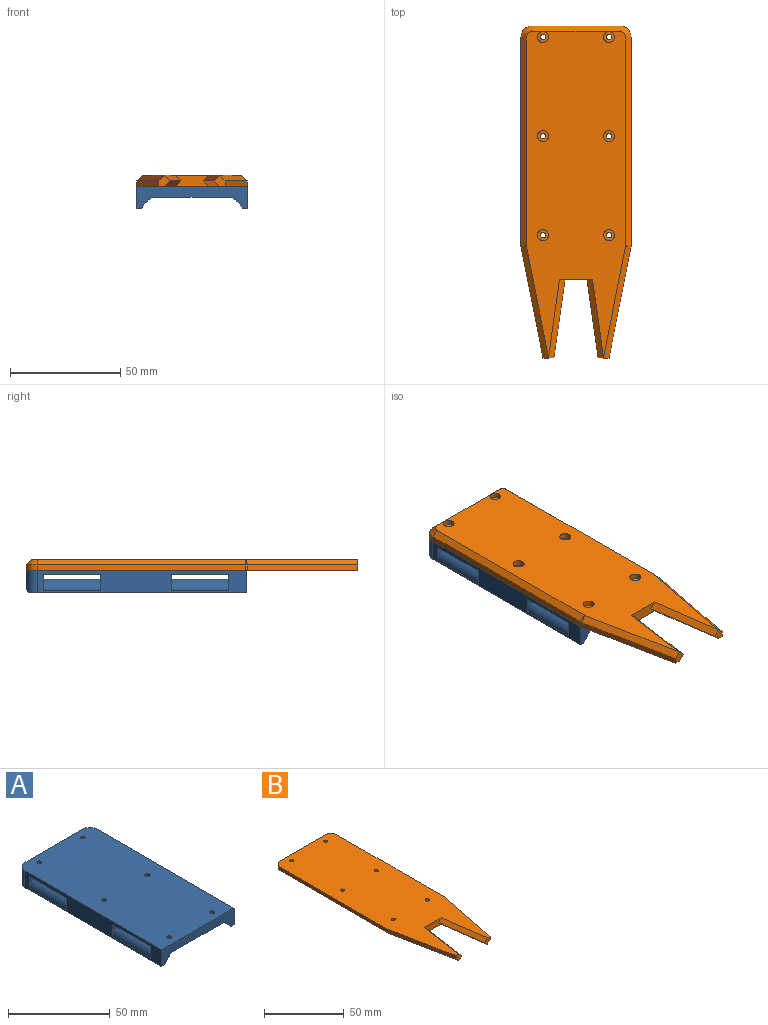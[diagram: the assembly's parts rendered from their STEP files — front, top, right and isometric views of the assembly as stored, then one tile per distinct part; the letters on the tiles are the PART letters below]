
ASSEMBLY  parts=2 mates=1
PART A: 30 faces, bbox 50x100x10.1 mm
  f0: plane 95x10.08mm, normal (1,0,0), area 589.4mm2, adj f4,f7,f15,f16,f17,f18,f20,f21
  f1: plane 95x10.08mm, normal (-1,0,0), area 589.4mm2, adj f4,f7,f15,f16,f17,f18,f20,f21
  f2: cylinder r=16.27mm len=100mm, axis (0,1,0), area 704.3mm2, adj f4,f5,f6,f27,f29
  f3: cylinder r=16.27mm len=100mm, axis (0,1,0), area 704.3mm2, adj f4,f5,f6,f26,f28
  f4: plane 50x10.08mm, normal (0,-1,0), area 290.8mm2, adj f0,f1,f2,f3,f6,f7,f26,f27
  f5: plane 40x6.39mm, normal (0,1,0), area 202.4mm2, adj f2,f3,f6,f7,f28,f29
  f6: plane 100x36.44mm, normal (0,0,-1), area 3614mm2, adj f2,f3,f4,f5,f8,f9,f10,f11
  f7: plane 100x50mm, normal (0,0,1), area 4959.8mm2, adj f0,f1,f4,f5,f8,f9,f10,f11
  f8: cylinder r=1.25mm len=5mm, axis (0,0,1), area 39.3mm2, adj f6,f7
  f9: cylinder r=1.25mm len=5mm, axis (0,0,1), area 39.3mm2, adj f6,f7
  f10: cylinder r=1.25mm len=5mm, axis (0,0,1), area 39.3mm2, adj f6,f7
  f11: cylinder r=1.25mm len=5mm, axis (0,0,1), area 39.3mm2, adj f6,f7
  f12: cylinder r=1.25mm len=5mm, axis (0,0,1), area 39.3mm2, adj f6,f7
  f13: cylinder r=1.25mm len=5mm, axis (0,0,1), area 39.3mm2, adj f6,f7
  f14: plane 39.84x26mm, normal (0,0,1), area 1035.8mm2, adj f15,f17,f23,f24
  f15: plane 50x7.08mm, normal (0,-1,0), area 111.1mm2, adj f0,f1,f14,f16,f23,f24
  f16: plane 50x26mm, normal (0,0,-1), area 1300mm2, adj f0,f1,f15,f17
  f17: plane 50x7.08mm, normal (0,1,0), area 111.1mm2, adj f0,f1,f14,f16,f23,f24
  f18: plane 50x7.08mm, normal (0,1,0), area 111.1mm2, adj f0,f1,f19,f21,f22,f25
  f19: plane 39.84x26mm, normal (0,0,1), area 1035.8mm2, adj f18,f20,f22,f25
  f20: plane 50x7.08mm, normal (0,-1,0), area 111.1mm2, adj f0,f1,f19,f21,f22,f25
  f21: plane 50x26mm, normal (0,0,-1), area 1300mm2, adj f0,f1,f18,f20
  f22: cylinder r=5.08mm len=26mm, axis (0,1,0), area 207.5mm2, adj f1,f18,f19,f20
  f23: cylinder r=5.08mm len=26mm, axis (0,1,0), area 207.5mm2, adj f1,f14,f15,f17
  f24: cylinder r=5.08mm len=26mm, axis (0,-1,0), area 207.5mm2, adj f0,f14,f15,f17
  f25: cylinder r=5.08mm len=26mm, axis (0,-1,0), area 207.5mm2, adj f0,f18,f19,f20
  f26: plane 98.97x1.96mm, normal (0,0,-1), area 191.6mm2, adj f0,f3,f4,f28
  f27: plane 98.97x1.96mm, normal (0,0,-1), area 191.6mm2, adj f1,f2,f4,f29
  f28: cylinder r=5mm len=10.08mm, axis (0,0,1), area 72.8mm2, adj f0,f3,f5,f7,f26
  f29: cylinder r=5mm len=10.08mm, axis (0,0,-1), area 72.8mm2, adj f1,f2,f5,f7,f27
PART B: 45 faces, bbox 50x150.8x5 mm
  f0: plane 94.51x2.5mm, normal (-1,0,0), area 236.3mm2, adj f8,f28,f31,f36
  f1: plane 50.31x9.91mm, normal (-0.98,-0.19,0), area 128.2mm2, adj f2,f8,f28,f34
  f2: plane 5x4.96mm, normal (0,-1,0), area 15.5mm2, adj f1,f8,f32,f33,f34
  f3: plane 15.05x5mm, normal (0,-1,0), area 62.6mm2, adj f8,f9,f32,f33,f40,f42
  f4: plane 5x4.96mm, normal (0,-1,0), area 15.5mm2, adj f5,f8,f40,f42,f44
  f5: plane 50.31x9.91mm, normal (0.98,-0.19,0), area 128.2mm2, adj f4,f8,f29,f44
  f6: plane 94.51x2.5mm, normal (1,0,0), area 236.3mm2, adj f8,f29,f30,f41
  f7: plane 40x2.5mm, normal (0,1,0), area 100mm2, adj f8,f30,f31,f38
  f8: plane 150.79x50mm, normal (0,0,1), area 6273.2mm2, adj f0,f1,f2,f3,f4,f5,f6,f7
  f9: plane 148.07x45mm, normal (0,0,-1), area 5321.6mm2, adj f3,f12,f15,f18,f21,f24,f27,f33
  f10: cylinder r=1.25mm len=2.5mm, axis (0,0,-1), area 19.6mm2, adj f8,f11
  f11: plane 5x5mm, normal (0,0,-1), area 14.7mm2, adj f10,f12
  f12: cylinder r=2.5mm len=5mm, axis (0,0,-1), area 39.3mm2, adj f9,f11
  f13: cylinder r=1.25mm len=2.5mm, axis (0,0,-1), area 19.6mm2, adj f8,f14
  f14: plane 5x5mm, normal (0,0,-1), area 14.7mm2, adj f13,f15
  f15: cylinder r=2.5mm len=5mm, axis (0,0,-1), area 39.3mm2, adj f9,f14
  f16: cylinder r=1.25mm len=2.5mm, axis (0,0,-1), area 19.6mm2, adj f8,f17
  f17: plane 5x5mm, normal (0,0,-1), area 14.7mm2, adj f16,f18
  f18: cylinder r=2.5mm len=5mm, axis (0,0,-1), area 39.3mm2, adj f9,f17
  f19: cylinder r=1.25mm len=2.5mm, axis (0,0,-1), area 19.6mm2, adj f8,f20
  f20: plane 5x5mm, normal (0,0,-1), area 14.7mm2, adj f19,f21
  f21: cylinder r=2.5mm len=5mm, axis (0,0,-1), area 39.3mm2, adj f9,f20
  f22: cylinder r=1.25mm len=2.5mm, axis (0,0,-1), area 19.6mm2, adj f8,f23
  f23: plane 5x5mm, normal (0,0,-1), area 14.7mm2, adj f22,f24
  f24: cylinder r=2.5mm len=5mm, axis (0,0,-1), area 39.3mm2, adj f9,f23
  f25: cylinder r=1.25mm len=2.5mm, axis (0,0,-1), area 19.6mm2, adj f8,f26
  f26: plane 5x5mm, normal (0,0,-1), area 14.7mm2, adj f25,f27
  f27: cylinder r=2.5mm len=5mm, axis (0,0,-1), area 39.3mm2, adj f9,f26
  f28: cylinder r=5mm len=2.5mm, axis (0,0,-1), area 2.4mm2, adj f0,f1,f8,f35
  f29: cylinder r=5mm len=2.5mm, axis (0,0,1), area 2.4mm2, adj f5,f6,f8,f43
  f30: cylinder r=5mm len=5mm, axis (0,0,-1), area 19.6mm2, adj f6,f7,f8,f39
  f31: cylinder r=5mm len=5mm, axis (0,0,1), area 19.6mm2, adj f0,f7,f8,f37
  f32: plane 35.82x7.52mm, normal (0.7,-0.1,0.71), area 127.9mm2, adj f2,f3,f8,f33
  f33: plane 35.82x7.49mm, normal (0.7,-0.1,-0.71), area 127.9mm2, adj f2,f3,f9,f32,f34
  f34: plane 50.79x12.42mm, normal (-0.69,-0.14,-0.71), area 182.1mm2, adj f1,f2,f9,f33,f35
  f35: cone r=2.5mm half-angle=45deg, axis (0,0,1), area 2.6mm2, adj f9,f28,f34,f36
  f36: plane 94.51x2.5mm, normal (-0.71,0,-0.71), area 334.2mm2, adj f0,f9,f35,f37
  f37: cone r=2.5mm half-angle=45deg, axis (0,0,1), area 20.8mm2, adj f9,f31,f36,f38
  f38: plane 40x2.5mm, normal (0,0.71,-0.71), area 141.4mm2, adj f7,f9,f37,f39
  f39: cone r=2.5mm half-angle=45deg, axis (0,0,1), area 20.8mm2, adj f9,f30,f38,f41
  f40: plane 35.82x7.52mm, normal (-0.7,-0.1,0.71), area 127.9mm2, adj f3,f4,f8,f42
  f41: plane 94.51x2.5mm, normal (0.71,0,-0.71), area 334.2mm2, adj f6,f9,f39,f43
  f42: plane 35.82x7.49mm, normal (-0.7,-0.1,-0.71), area 127.9mm2, adj f3,f4,f9,f40,f44
  f43: cone r=2.5mm half-angle=45deg, axis (0,0,1), area 2.6mm2, adj f9,f29,f41,f44
  f44: plane 50.79x12.42mm, normal (0.69,-0.14,-0.71), area 182.1mm2, adj f4,f5,f9,f42,f43
PLACE A t=(-42.3,10.83,-3.19)mm
PLACE B rot(axis=(0,1,0),180deg) t=(-42.3,-28.85,26.81)mm
MATE fastened B.f25 <-> A.f8  axis (0,0,-1) through (-57.3,5.83,21.81)mm
